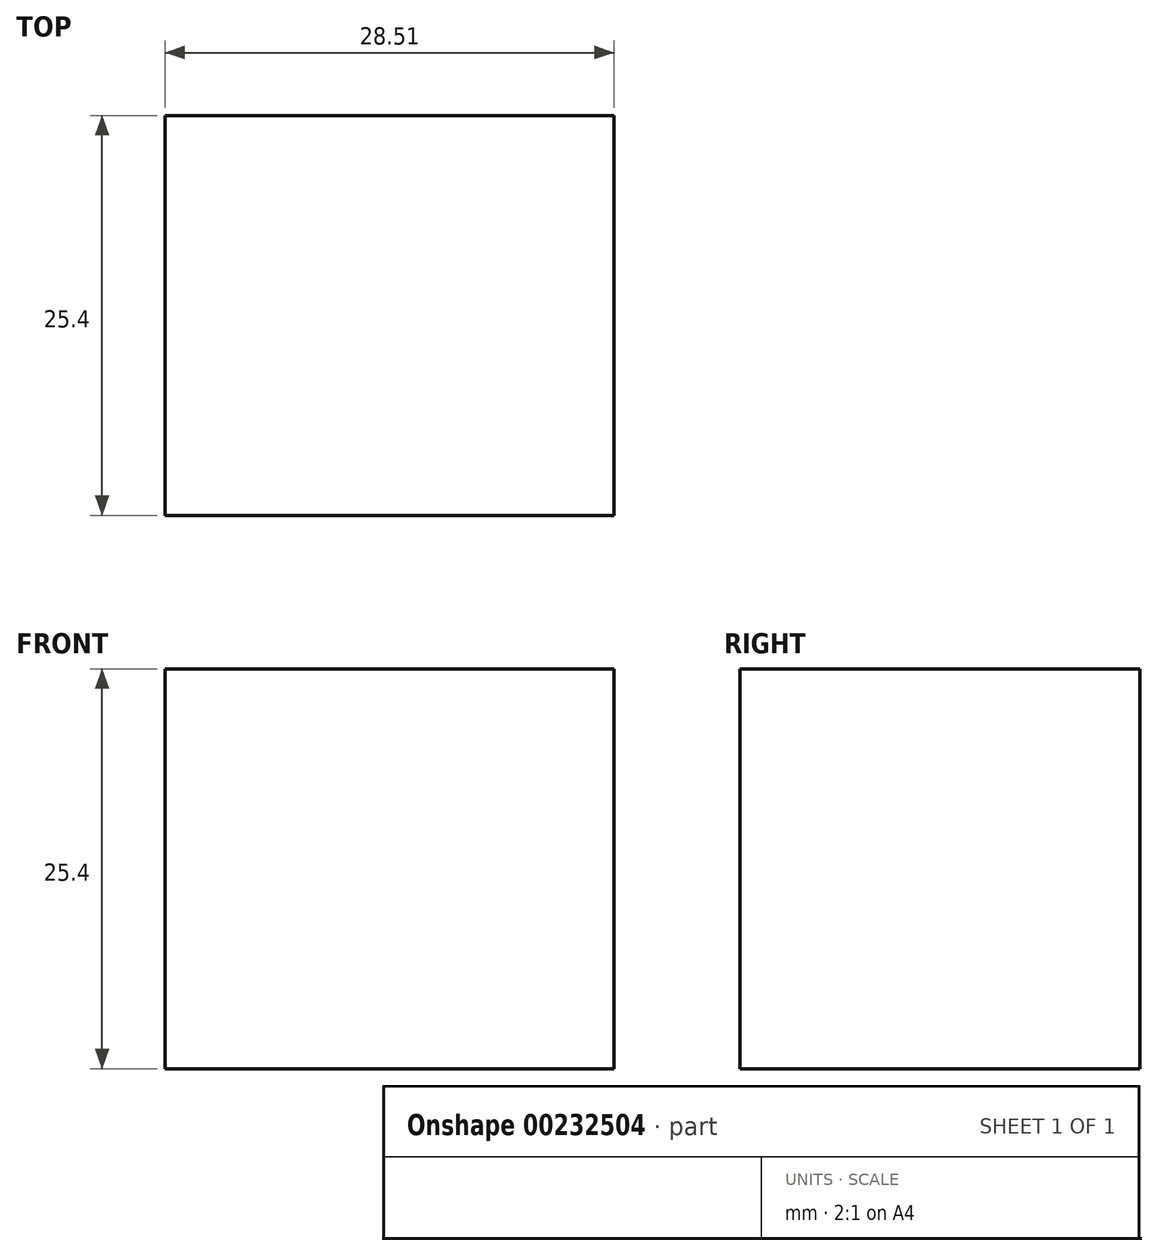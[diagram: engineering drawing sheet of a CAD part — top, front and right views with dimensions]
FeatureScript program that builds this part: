
annotation { "Feature Type Name" : "Feature", "Feature Type Description" : "" }
export const myFeature = defineFeature(function(context is Context, id is Id, definition is map)
    precondition{}
    {
        {
            var Q0;
            Q0=qCreatedBy(makeId("Front.planeOp"),FACE);
            var sketch = newSketch(context, id + "F0", { "sketchPlane" : qUnion([Q0])});
            skLineSegment(sketch, "E0", {"start": v(0, 0) * mm, "end": v(0, 25.4) * mm});
            skLineSegment(sketch, "E1", {"start": v(0, 25.4) * mm, "end": v(28.51, 25.4) * mm});
            skLineSegment(sketch, "E2", {"start": v(28.51, 25.4) * mm, "end": v(28.51, 0) * mm});
            skLineSegment(sketch, "E3", {"start": v(0, 0) * mm, "end": v(28.51, 0) * mm});
            skSolve(sketch);
        }
        {
            var Q0;
            Q0=makeQuery(id+"F0.imprint","IMPRINT",FACE,{"disambiguationData":[TD([[makeQuery(id+"F0.imprint","IMPRINT",EDGE,{"derivedFrom":sQuery(id+"F0.wireOp",EDGE,"E0")}),-1.0]])]});
            extrude(context, id + "F1", {"entities" : qUnion([Q0]), "depth" : 25.4 * mm});
        }
    });
